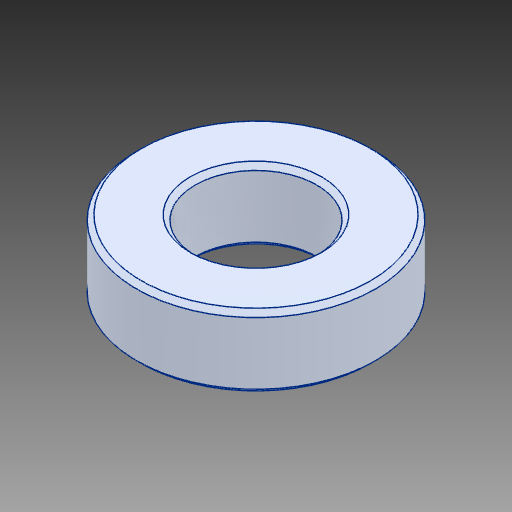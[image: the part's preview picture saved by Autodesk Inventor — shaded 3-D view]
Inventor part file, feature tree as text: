
AUTODESK INVENTOR PART (.ipt)
format: ipt  version: 2017 (Build 210142000, 142)  size: 111,104 bytes
history: mixed  units: mm
features: chamfer x1, imported_body x1
ambient origin geometry x8: Origin, YZ Plane, XZ Plane, XY Plane, X Axis, Y Axis, Z Axis, Center Point
bodies: Solid1 (imported_parasolid)
feature tree (2):
  chamfer  "Chamfer1"  [1 undecoded]
  imported_body  NMx_Import_Brep_tag  [imported B-rep: ~8 faces, bbox_mm=[2.45, 0.0, 3.0]]
note: 1 required parameter value undecoded (feature->parameter linkage not recoverable at this tier; creation-order binding heuristic only, values carry confidence <= 0.55)
